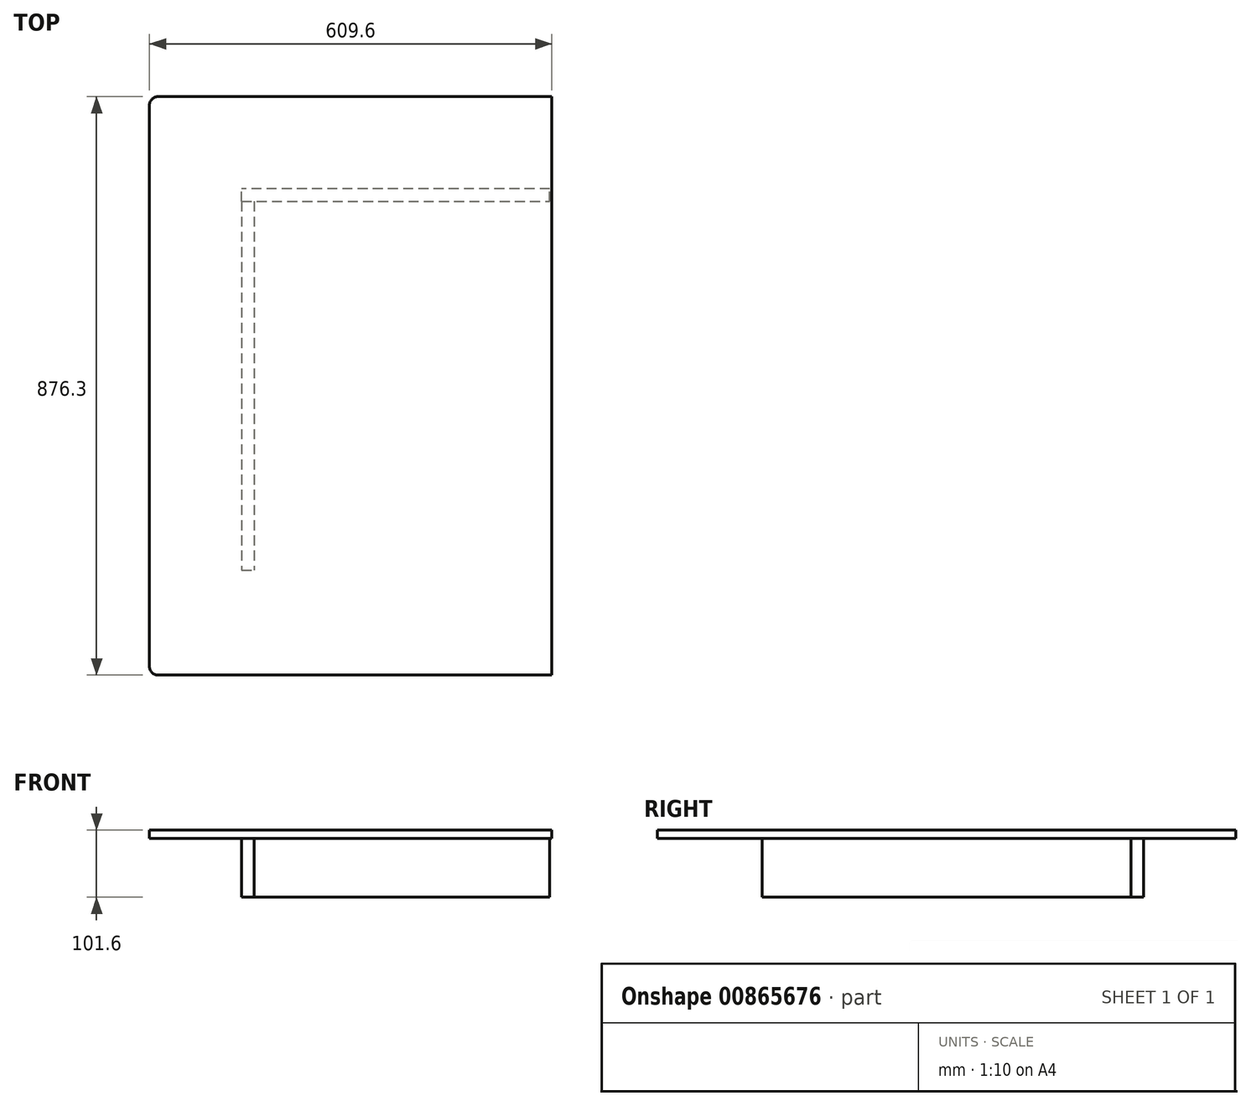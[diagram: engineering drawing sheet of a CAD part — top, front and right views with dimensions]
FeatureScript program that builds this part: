
annotation { "Feature Type Name" : "Feature", "Feature Type Description" : "" }
export const myFeature = defineFeature(function(context is Context, id is Id, definition is map)
    precondition{}
    {
        {
            var Q0;
            Q0=qCreatedBy(makeId("Top.planeOp"),FACE);
            var sketch = newSketch(context, id + "F0", { "sketchPlane" : qUnion([Q0])});
            skLineSegment(sketch, "E0.bottom", {"start": v(609.6, 438.15) * mm, "end": v(-609.6, 438.15) * mm});
            skLineSegment(sketch, "E0.top", {"start": v(609.6, -438.15) * mm, "end": v(-609.6, -438.15) * mm});
            skLineSegment(sketch, "E0.left", {"start": v(609.6, 438.15) * mm, "end": v(609.6, -438.15) * mm});
            skLineSegment(sketch, "E0.right", {"start": v(-609.6, 438.15) * mm, "end": v(-609.6, -438.15) * mm});
            skPoint(sketch, "E0.middle", {"position": v(0, 0) * mm});
            skLineSegment(sketch, "E1.bottom", {"start": v(-469.9, 279.4) * mm, "end": v(-450.85, 279.4) * mm});
            skLineSegment(sketch, "E1.top", {"start": v(-469.9, -279.4) * mm, "end": v(-450.85, -279.4) * mm});
            skLineSegment(sketch, "E1.left", {"start": v(-469.9, 279.4) * mm, "end": v(-469.9, -279.4) * mm});
            skLineSegment(sketch, "E1.right", {"start": v(-450.85, 279.4) * mm, "end": v(-450.85, -279.4) * mm});
            skLineSegment(sketch, "E2.bottom", {"start": v(-469.9, -279.4) * mm, "end": v(469.9, -279.4) * mm});
            skLineSegment(sketch, "E2.top", {"start": v(-469.9, -298.45) * mm, "end": v(469.9, -298.45) * mm});
            skLineSegment(sketch, "E2.left", {"start": v(-469.9, -279.4) * mm, "end": v(-469.9, -298.45) * mm});
            skLineSegment(sketch, "E2.right", {"start": v(469.9, -279.4) * mm, "end": v(469.9, -298.45) * mm});
            skLineSegment(sketch, "E3.bottom", {"start": v(469.9, -279.4) * mm, "end": v(450.85, -279.4) * mm});
            skLineSegment(sketch, "E3.top", {"start": v(469.9, 279.4) * mm, "end": v(450.85, 279.4) * mm});
            skLineSegment(sketch, "E3.left", {"start": v(469.9, -279.4) * mm, "end": v(469.9, 279.4) * mm});
            skLineSegment(sketch, "E3.right", {"start": v(450.85, -279.4) * mm, "end": v(450.85, 279.4) * mm});
            skLineSegment(sketch, "E4.bottom", {"start": v(469.9, 279.4) * mm, "end": v(-469.9, 279.4) * mm});
            skLineSegment(sketch, "E4.top", {"start": v(469.9, 298.45) * mm, "end": v(-469.9, 298.45) * mm});
            skLineSegment(sketch, "E4.left", {"start": v(469.9, 279.4) * mm, "end": v(469.9, 298.45) * mm});
            skLineSegment(sketch, "E4.right", {"start": v(-469.9, 279.4) * mm, "end": v(-469.9, 298.45) * mm});
            skLineSegment(sketch, "E5.bottom", {"start": v(-22.15, 279.4) * mm, "end": v(-3.1, 279.4) * mm});
            skLineSegment(sketch, "E5.top", {"start": v(-22.15, -279.4) * mm, "end": v(-3.1, -279.4) * mm});
            skLineSegment(sketch, "E5.left", {"start": v(-22.15, 279.4) * mm, "end": v(-22.15, -279.4) * mm});
            skLineSegment(sketch, "E5.right", {"start": v(-3.1, 279.4) * mm, "end": v(-3.1, -279.4) * mm});
            skLineSegment(sketch, "E6", {"start": v(0, 0) * mm, "end": v(0, 478.35) * mm, "construction": true});
            skPoint(sketch, "E6.endSnap0", {"position": v(0, 438.15) * mm});
            skLineSegment(sketch, "E7", {"start": v(-3.1, 279.4) * mm, "end": v(-3.1, 298.45) * mm});
            skSolve(sketch);
        }
        {
            var Q0;
            {var subQ0=sQuery(id+"F0.wireOp",EDGE,"E4.right");Q0=makeQuery(id+"F0.imprint","IMPRINT",FACE,{"disambiguationData":[TD([[makeQuery(id+"F0.imprint","IMPRINT",EDGE,{"derivedFrom":subQ0}),-1.0]])]});}
            extrude(context, id + "F1", {"entities" : qUnion([Q0]), "oppositeDirection" : true, "depth" : 88.9 * mm, "offsetDistance" : 25.4 * mm});
        }
        {
            var Q0;
            {var subQ0=sQuery(id+"F0.wireOp",EDGE,"E1.left");Q0=makeQuery(id+"F0.imprint","IMPRINT",FACE,{"disambiguationData":[TD([[makeQuery(id+"F0.imprint","IMPRINT",EDGE,{"derivedFrom":subQ0}),1.0]])]});}
            var Q1;
            Q1=makeQuery(id+"F1.opExtrude","CAP_VERTEX",VERTEX,{"disambiguationData":[OSD([sQuery(id+"F0.wireOp",EDGE,"E1.left"),sQuery(id+"F0.wireOp",EDGE,"E4.bottom"),sQuery(id+"F0.wireOp",EDGE,"E4.right")])],"isStart":false});
            extrude(context, id + "F2", {"entities" : qUnion([Q0]), "endBound" : BoundingType.UP_TO_VERTEX, "oppositeDirection" : true, "depth" : 25.4 * mm, "endBoundEntityVertex" : qUnion([Q1]), "offsetDistance" : 25.4 * mm});
        }
        {
            var Q0;
            Q0=qCreatedBy(makeId("Top.planeOp"),FACE);
            var sketch = newSketch(context, id + "F3", { "sketchPlane" : qUnion([Q0])});
            skLineSegment(sketch, "E8.0", {"start": v(-609.6, 438.15) * mm, "end": v(-609.6, -438.15) * mm});
            skLineSegment(sketch, "E9.0", {"start": v(0, 438.15) * mm, "end": v(-609.6, 438.15) * mm});
            skLineSegment(sketch, "E10.0", {"start": v(0, -438.15) * mm, "end": v(-609.6, -438.15) * mm});
            skLineSegment(sketch, "E11", {"start": v(0, 438.15) * mm, "end": v(0, -438.15) * mm});
            skSolve(sketch);
        }
        {
            var Q0;
            Q0=makeQuery(id+"F3.imprint","IMPRINT",FACE,{"disambiguationData":[TD([[makeQuery(id+"F3.imprint","IMPRINT",EDGE,{"derivedFrom":sQuery(id+"F3.wireOp",EDGE,"E8.0")}),1.0]])]});
            extrude(context, id + "F4", {"entities" : qUnion([Q0]), "depth" : 12.7 * mm, "offsetDistance" : 25.4 * mm});
        }
        {
            var Q0;
            Q0=makeQuery(id+"F4.opExtrude","SWEPT_EDGE",EDGE,{"disambiguationData":[OSD([sQuery(id+"F3.wireOp",EDGE,"E8.0"),sQuery(id+"F3.wireOp",EDGE,"E10.0")])]});
            var Q1;
            Q1=makeQuery(id+"F4.opExtrude","SWEPT_EDGE",EDGE,{"disambiguationData":[OSD([sQuery(id+"F3.wireOp",EDGE,"E8.0"),sQuery(id+"F3.wireOp",EDGE,"E9.0")])]});
            fillet(context, id + "F5", {"entities" : qUnion([Q0, Q1]), "radius" : 12.7 * mm, "tangentPropagation" : true, "allowEdgeOverflow" : false});
        }
    });
